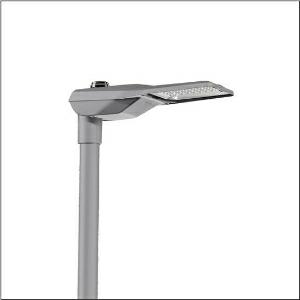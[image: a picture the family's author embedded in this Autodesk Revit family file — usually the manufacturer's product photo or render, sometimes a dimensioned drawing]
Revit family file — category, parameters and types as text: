
# Revit family: streetlight_sl_21_mini___pl52_5xe6h37n08hb_79bc
name_source: partatom
category: Lighting Fixtures
units: mm (PartAtom-declared; Revit-internal decimal feet)

## family parameters
Cut with Voids When Loaded = No
Host = Face
Light Source = No
Part Type = Normal
Room Calculation Point = No
Round Connector Dimension = Use Diameter
Shared = No

## types (1)
- --- (1 x LED, 8890 lm, 66 W, 3000K)
    Apparent Load = 66 VA
    CIE Flux Codes = 27 59 98 100 100
    Color Rendering = 70
    Color Temperature = 3000K
    Default Elevation = 1800 mm
    Description = Streetlight SL 21 mini, mast luminaire, primary light control with lens, of PMMA, primary optical cover: cover, of toughened safety glass, transparent, light distribution: PL52, light emission: direct distribution, primary light characteristic: asymmetric, installation type: side-entry, LED, 3G 1.5mm², High Power LED, rated luminous flux: 8.890lm, luminous efficacy: 135lm/W, light colour: 730, colour temperature: 3000K, control gear: NEMA (7pin), control: overheat protection, pre-setting: linear dimming characteristic, constant luminous flux control, time-dependent luminous flux control, flexible luminous flux parameterisation, mains connection: 230..240V, AC, 50/60Hz, connection cable pre-assembled, cable length: 8,5m, wiring characteristics: H07RN-F, start of lifetime: 66W, end of service life: 69W, reduction: 30W, luminaire housing, of diecast aluminium (EN AC-44300), powder-coated, Siteco® metallic grey (DB 702S), corrosivity category C5 mid according to DIN EN ISO 12944, multi-level sealing system, sealing non-destructively replaceable, inclination adjustable: 0°, 5°, 10°, 15°, length: 628mm, width: 235mm, height: 110mm, spigot size: 42mm (side-entry), mounting height: 4..8m, protection rating (complete): IP66, insulation class (complete): insulation class I (protective earthing), certification: CE, ENEC, ENEC+, VDE, impact resistance: IK10, permissible operating ambient temperature for outdoor applications: -40..+50°C, standard-compliant lighting for roads and squares, packaging unit: 1 piece

Light Distribution: PL52
    Height = 110 mm
    Lamp = 1 x LED
    Lamp Light Flux = 8890 lm
    Lamp Power = 66 W
    Lamp count = 1
    Length = 625 mm
    Luminous efficacy = 135 lm/W
    Manufacturer = Siteco
    ModVariant = No
    Model = 5XE6H37N08HB
    Number of Poles = 1
    OnlyDefault = Yes
    Power Factor = 1
    Product Name = Streetlight SL 21 mini | PL52
    Product group = mast luminaire | pylon top
    ProductGroupID = 6100
    Protection Class = Protection class I
    Protection Degree = IP 66
    RLX_Detail_Level = 1
    RLX_Emergency_Light_Flux = 0 lm
    RLX_Emergency_Type = 0
    RLX_Emergency_Type_DB = No
    RlxData = <blob elided: 35733 chars, md5=23dd6ef4>
    Socket = socket
    Standby Power = 0 W
    System Light Flux = 8890 lm
    System Power = 66 W
    Type Comments = factory setting: luminous flux: 100 % | dim-lin: 254 | 670 mA
    Type Image = l_1294379.jpg
    URL = http://relux.com
    VarID = @adj_158523
    Voltage = 0 V
    Weight = 0.00 kg
    Width = 234 mm

## geometry (parser evidence)
native form markers: Blend x4, Sweep x9
no freeform markers — native parametric forms only
